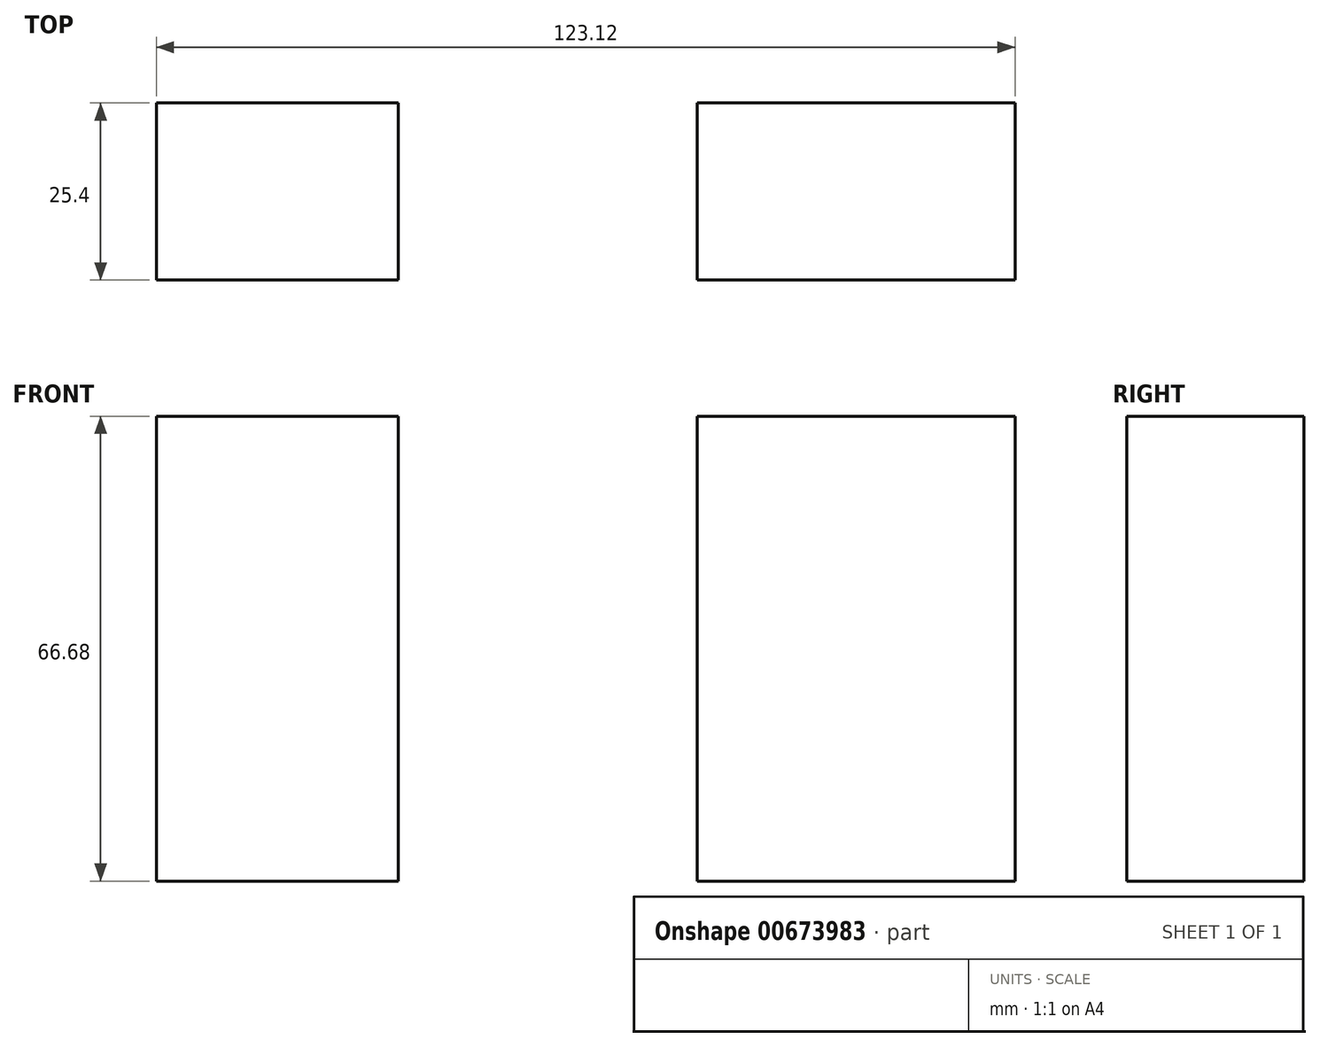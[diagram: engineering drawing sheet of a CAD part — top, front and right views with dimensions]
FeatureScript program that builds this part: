
annotation { "Feature Type Name" : "Feature", "Feature Type Description" : "" }
export const myFeature = defineFeature(function(context is Context, id is Id, definition is map)
    precondition{}
    {
        {
            var Q0;
            Q0=qCreatedBy(makeId("Front.planeOp"),FACE);
            var sketch = newSketch(context, id + "F0", { "sketchPlane" : qUnion([Q0])});
            skLineSegment(sketch, "E0.bottom", {"start": v(-61.45, 28.34) * mm, "end": v(61.67, 28.34) * mm});
            skLineSegment(sketch, "E0.top", {"start": v(-61.45, -38.34) * mm, "end": v(61.67, -38.34) * mm});
            skLineSegment(sketch, "E0.left", {"start": v(-61.45, 28.34) * mm, "end": v(-61.45, -38.34) * mm});
            skLineSegment(sketch, "E0.right", {"start": v(61.67, 28.34) * mm, "end": v(61.67, -38.34) * mm});
            skSolve(sketch);
        }
        {
            var Q0;
            Q0=makeQuery(id+"F0.imprint","IMPRINT",FACE,{"disambiguationData":[TD([[makeQuery(id+"F0.imprint","IMPRINT",EDGE,{"derivedFrom":sQuery(id+"F0.wireOp",EDGE,"E0.bottom")}),-1.0]])]});
            extrude(context, id + "F1", {"entities" : qUnion([Q0]), "depth" : 25.4 * mm, "offsetDistance" : 25.4 * mm});
        }
        {
            var Q0;
            Q0=makeQuery(id+"F1.opExtrude","CAP_FACE",FACE,{"disambiguationData":[OSD([sQuery(id+"F0.wireOp",EDGE,"E0.bottom"),sQuery(id+"F0.wireOp",EDGE,"E0.top"),sQuery(id+"F0.wireOp",EDGE,"E0.left"),sQuery(id+"F0.wireOp",EDGE,"E0.right")])],"isStart":false});
            var sketch = newSketch(context, id + "F2", { "sketchPlane" : qUnion([Q0])});
            skLineSegment(sketch, "E1.bottom", {"start": v(-26.78, 46.56) * mm, "end": v(16.11, 46.56) * mm});
            skLineSegment(sketch, "E1.top", {"start": v(-26.78, -59) * mm, "end": v(16.11, -59) * mm});
            skLineSegment(sketch, "E1.left", {"start": v(-26.78, 46.56) * mm, "end": v(-26.78, -59) * mm});
            skLineSegment(sketch, "E1.right", {"start": v(16.11, 46.56) * mm, "end": v(16.11, -59) * mm});
            skSolve(sketch);
        }
        {
            var Q0;
            {var subQ0=sQuery(id+"F2.wireOp",EDGE,"E1.left");var subQ1=makeQuery(id+"F1.opExtrude","CAP_EDGE",EDGE,{"disambiguationData":[OSD([sQuery(id+"F0.wireOp",EDGE,"E0.bottom")])],"isStart":false});var subQ2=makeQuery(id+"F2.imprint","INTERSECT",VERTEX,{"derivedFrom":[subQ1,subQ0]});Q0=makeQuery(id+"F2.imprint","IMPRINT",FACE,{"disambiguationData":[TD([[makeQuery(id+"F2.imprint","IMPRINT",EDGE,{"disambiguationData":[TD([[subQ2,-1.0]])],"derivedFrom":subQ0}),1.0]])]});}
            extrude(context, id + "F3", {"entities" : qUnion([Q0]), "operationType" : NewBodyOperationType.REMOVE, "oppositeDirection" : true, "depth" : 25.4 * mm, "offsetDistance" : 25.4 * mm});
        }
    });
